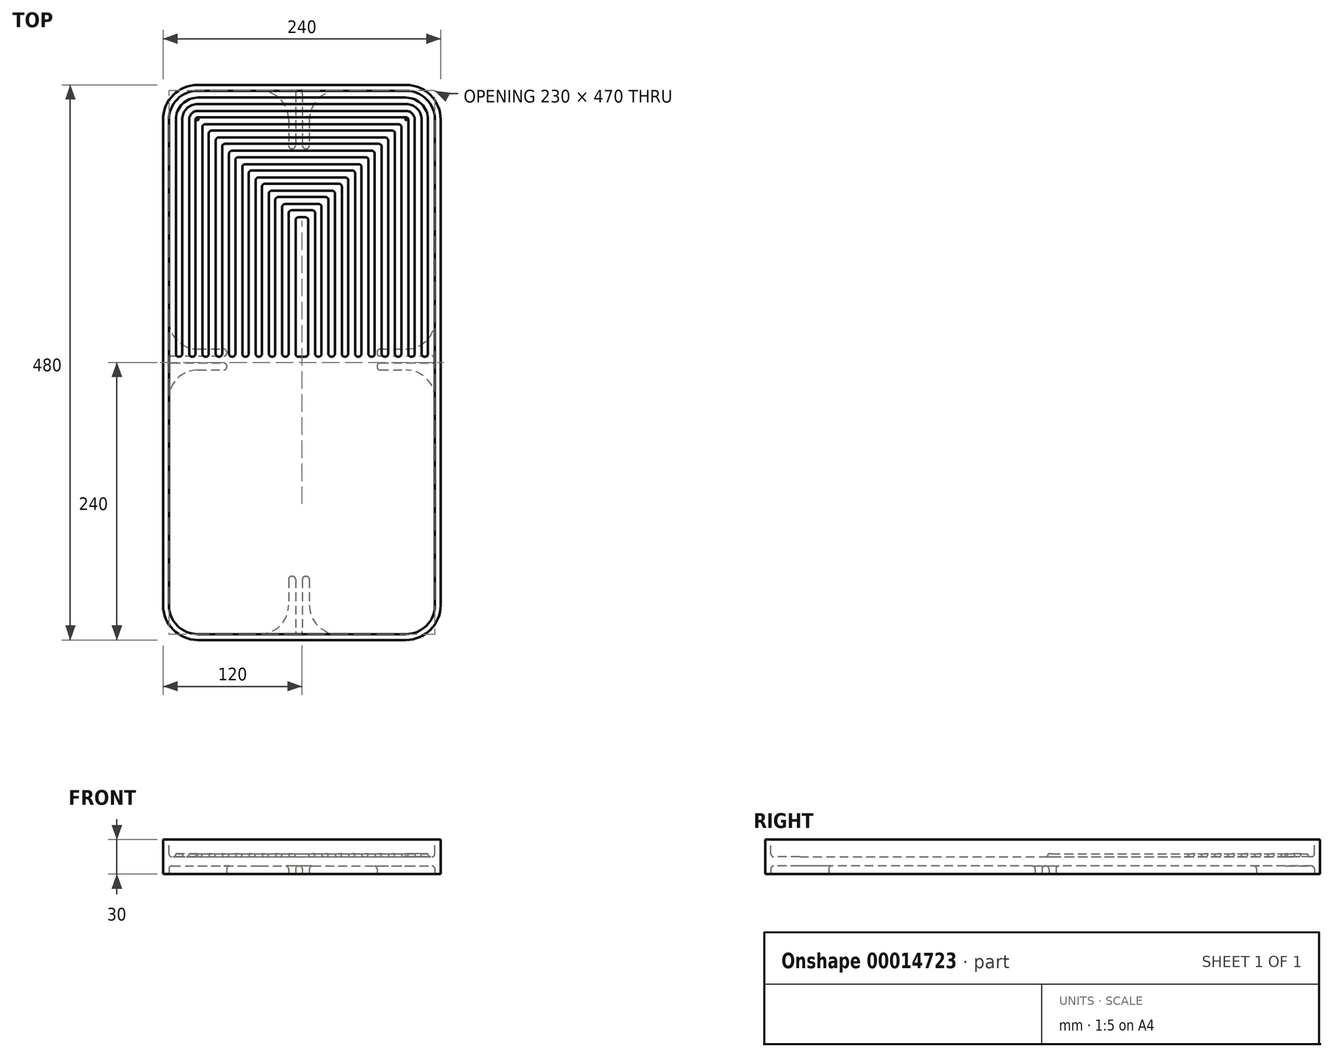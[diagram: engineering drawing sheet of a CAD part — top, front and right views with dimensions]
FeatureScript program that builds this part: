
annotation { "Feature Type Name" : "Feature", "Feature Type Description" : "" }
export const myFeature = defineFeature(function(context is Context, id is Id, definition is map)
    precondition{}
    {
        {
            var Q0;
            Q0=qCreatedBy(makeId("Top.planeOp"),FACE);
            var sketch = newSketch(context, id + "F0", { "sketchPlane" : qUnion([Q0])});
            skLineSegment(sketch, "E0.rect.bottom", {"start": v(-90, 240) * mm, "end": v(90, 240) * mm});
            skLineSegment(sketch, "E0.rect.top", {"start": v(-90, -240) * mm, "end": v(90, -240) * mm});
            skLineSegment(sketch, "E0.rect.left", {"start": v(-120, 210) * mm, "end": v(-120, -210) * mm});
            skLineSegment(sketch, "E0.rect.right", {"start": v(120, 210) * mm, "end": v(120, -210) * mm});
            skPoint(sketch, "E0.rect.middle", {"position": v(0, 0) * mm});
            skPoint(sketch, "E1.visualSharp", {"position": v(-120, 240) * mm});
            skArc(sketch, "E1.filletArc", {"start": v(-90, 240) * mm, "mid": v(-111.21, 231.21) * mm, "end": v(-120, 210) * mm});
            skPoint(sketch, "E2.visualSharp", {"position": v(120, 240) * mm});
            skArc(sketch, "E2.filletArc", {"start": v(120, 210) * mm, "mid": v(111.21, 231.21) * mm, "end": v(90, 240) * mm});
            skPoint(sketch, "E3.visualSharp", {"position": v(120, -240) * mm});
            skArc(sketch, "E3.filletArc", {"start": v(90, -240) * mm, "mid": v(111.21, -231.21) * mm, "end": v(120, -210) * mm});
            skPoint(sketch, "E4.visualSharp", {"position": v(-120, -240) * mm});
            skArc(sketch, "E4.filletArc", {"start": v(-120, -210) * mm, "mid": v(-111.21, -231.21) * mm, "end": v(-90, -240) * mm});
            skSolve(sketch);
        }
        {
            var Q0;
            Q0 = qSketchRegion(id + "F0", true);
            extrude(context, id + "F1", {"entities" : qUnion([Q0]), "depth" : 30 * mm});
        }
        {
            var Q0;
            Q0=makeQuery(id+"F1.opExtrude","CAP_FACE",FACE,{"disambiguationData":[OSD([sQuery(id+"F0.wireOp",EDGE,"E0.rect.bottom"),sQuery(id+"F0.wireOp",EDGE,"E0.rect.top"),sQuery(id+"F0.wireOp",EDGE,"E0.rect.left"),sQuery(id+"F0.wireOp",EDGE,"E0.rect.right"),sQuery(id+"F0.wireOp",EDGE,"E1.filletArc"),sQuery(id+"F0.wireOp",EDGE,"E2.filletArc"),sQuery(id+"F0.wireOp",EDGE,"E3.filletArc"),sQuery(id+"F0.wireOp",EDGE,"E4.filletArc")])],"isStart":true});
            var sketch = newSketch(context, id + "F2", { "sketchPlane" : qUnion([Q0])});
            skLineSegment(sketch, "E5.0", {"start": v(-90, -235) * mm, "end": v(-36.5, -235) * mm});
            skArc(sketch, "E5.1", {"start": v(115, -210) * mm, "mid": v(107.68, -227.68) * mm, "end": v(90, -235) * mm});
            skLineSegment(sketch, "E5.2", {"start": v(115, -210) * mm, "end": v(115, -36.5) * mm});
            skArc(sketch, "E5.3", {"start": v(90, 235) * mm, "mid": v(107.68, 227.68) * mm, "end": v(115, 210) * mm});
            skLineSegment(sketch, "E5.4", {"start": v(-90, 235) * mm, "end": v(-36.5, 235) * mm});
            skArc(sketch, "E5.5", {"start": v(-90, -235) * mm, "mid": v(-107.68, -227.68) * mm, "end": v(-115, -210) * mm});
            skArc(sketch, "E5.6", {"start": v(-115, 210) * mm, "mid": v(-107.68, 227.68) * mm, "end": v(-90, 235) * mm});
            skLineSegment(sketch, "E5.7", {"start": v(-115, -210) * mm, "end": v(-115, -36.5) * mm});
            skLineSegment(sketch, "E6", {"start": v(6.5, -210) * mm, "end": v(6.5, -187.5) * mm});
            skLineSegment(sketch, "E7.0", {"start": v(0.5, -232.5) * mm, "end": v(0.5, -187.5) * mm});
            skLineSegment(sketch, "E8.0", {"start": v(-5.5, -232.5) * mm, "end": v(-5.5, -187.5) * mm});
            skLineSegment(sketch, "E9.0", {"start": v(-11.5, -210) * mm, "end": v(-11.5, -187.5) * mm});
            skLineSegment(sketch, "E10.0", {"start": v(-9, -185) * mm, "end": v(-8, -185) * mm});
            skLineSegment(sketch, "E11.0", {"start": v(-9, 185) * mm, "end": v(-8, 185) * mm});
            skLineSegment(sketch, "E12.trimOffspring", {"start": v(-11.5, 187.5) * mm, "end": v(-11.5, 210) * mm});
            skLineSegment(sketch, "E13.trimOffspring", {"start": v(-5.5, 187.5) * mm, "end": v(-5.5, 232.5) * mm});
            skLineSegment(sketch, "E14.trimOffspring", {"start": v(0.5, 187.5) * mm, "end": v(0.5, 232.5) * mm});
            skLineSegment(sketch, "E15.trimOffspring", {"start": v(6.5, 187.5) * mm, "end": v(6.5, 210) * mm});
            skLineSegment(sketch, "E16.trimOffspring", {"start": v(3, 185) * mm, "end": v(4, 185) * mm});
            skLineSegment(sketch, "E17.trimOffspring", {"start": v(3, -185) * mm, "end": v(4, -185) * mm});
            skLineSegment(sketch, "E18.trimOffspring", {"start": v(-3, -235) * mm, "end": v(-2, -235) * mm});
            skLineSegment(sketch, "E19.trimOffspring", {"start": v(31.5, -235) * mm, "end": v(90, -235) * mm});
            skLineSegment(sketch, "E20.trimOffspring", {"start": v(-3, 235) * mm, "end": v(-2, 235) * mm});
            skLineSegment(sketch, "E21.trimOffspring", {"start": v(31.5, 235) * mm, "end": v(90, 235) * mm});
            skLineSegment(sketch, "E22", {"start": v(-90, -11.5) * mm, "end": v(-67.5, -11.5) * mm});
            skLineSegment(sketch, "E23.0", {"start": v(-112.5, -5.5) * mm, "end": v(-67.5, -5.5) * mm});
            skLineSegment(sketch, "E24.0", {"start": v(-112.5, 0.5) * mm, "end": v(-67.5, 0.5) * mm});
            skLineSegment(sketch, "E25.0", {"start": v(-90, 6.5) * mm, "end": v(-67.5, 6.5) * mm});
            skLineSegment(sketch, "E26.0", {"start": v(-65, -9) * mm, "end": v(-65, -8) * mm});
            skLineSegment(sketch, "E27.0", {"start": v(65, -9) * mm, "end": v(65, -8) * mm});
            skLineSegment(sketch, "E28.trimOffspring", {"start": v(67.5, 6.5) * mm, "end": v(90, 6.5) * mm});
            skLineSegment(sketch, "E29.trimOffspring", {"start": v(67.5, 0.5) * mm, "end": v(112.5, 0.5) * mm});
            skLineSegment(sketch, "E30.trimOffspring", {"start": v(67.5, -5.5) * mm, "end": v(112.5, -5.5) * mm});
            skLineSegment(sketch, "E31.trimOffspring", {"start": v(67.5, -11.5) * mm, "end": v(90, -11.5) * mm});
            skLineSegment(sketch, "E32.trimOffspring", {"start": v(65, 3) * mm, "end": v(65, 4) * mm});
            skLineSegment(sketch, "E33.trimOffspring", {"start": v(-65, 3) * mm, "end": v(-65, 4) * mm});
            skLineSegment(sketch, "E34.trimOffspring", {"start": v(-115, -3) * mm, "end": v(-115, -2) * mm});
            skLineSegment(sketch, "E35.trimOffspring", {"start": v(-115, 31.5) * mm, "end": v(-115, 210) * mm});
            skLineSegment(sketch, "E36.trimOffspring", {"start": v(115, -3) * mm, "end": v(115, -2) * mm});
            skLineSegment(sketch, "E37.trimOffspring", {"start": v(115, 31.5) * mm, "end": v(115, 210) * mm});
            skPoint(sketch, "E38.visualSharp", {"position": v(-11.5, -185) * mm});
            skArc(sketch, "E38.filletArc", {"start": v(-9, -185) * mm, "mid": v(-10.77, -185.73) * mm, "end": v(-11.5, -187.5) * mm});
            skPoint(sketch, "E39.visualSharp", {"position": v(-5.5, -185) * mm});
            skArc(sketch, "E39.filletArc", {"start": v(-5.5, -187.5) * mm, "mid": v(-6.23, -185.73) * mm, "end": v(-8, -185) * mm});
            skPoint(sketch, "E40.visualSharp", {"position": v(0.5, -185) * mm});
            skArc(sketch, "E40.filletArc", {"start": v(3, -185) * mm, "mid": v(1.23, -185.73) * mm, "end": v(0.5, -187.5) * mm});
            skPoint(sketch, "E41.visualSharp", {"position": v(6.5, -185) * mm});
            skArc(sketch, "E41.filletArc", {"start": v(6.5, -187.5) * mm, "mid": v(5.77, -185.73) * mm, "end": v(4, -185) * mm});
            skPoint(sketch, "E42.visualSharp", {"position": v(-5.5, -235) * mm});
            skArc(sketch, "E42.filletArc", {"start": v(-5.5, -232.5) * mm, "mid": v(-4.77, -234.27) * mm, "end": v(-3, -235) * mm});
            skPoint(sketch, "E43.visualSharp", {"position": v(0.5, -235) * mm});
            skArc(sketch, "E43.filletArc", {"start": v(-2, -235) * mm, "mid": v(-0.23, -234.27) * mm, "end": v(0.5, -232.5) * mm});
            skPoint(sketch, "E44.visualSharp", {"position": v(-5.5, 235) * mm});
            skArc(sketch, "E44.filletArc", {"start": v(-3, 235) * mm, "mid": v(-4.77, 234.27) * mm, "end": v(-5.5, 232.5) * mm});
            skPoint(sketch, "E45.visualSharp", {"position": v(0.5, 235) * mm});
            skArc(sketch, "E45.filletArc", {"start": v(0.5, 232.5) * mm, "mid": v(-0.23, 234.27) * mm, "end": v(-2, 235) * mm});
            skPoint(sketch, "E46.visualSharp", {"position": v(-11.5, 185) * mm});
            skArc(sketch, "E46.filletArc", {"start": v(-11.5, 187.5) * mm, "mid": v(-10.77, 185.73) * mm, "end": v(-9, 185) * mm});
            skPoint(sketch, "E47.visualSharp", {"position": v(-5.5, 185) * mm});
            skArc(sketch, "E47.filletArc", {"start": v(-8, 185) * mm, "mid": v(-6.23, 185.73) * mm, "end": v(-5.5, 187.5) * mm});
            skPoint(sketch, "E48.visualSharp", {"position": v(0.5, 185) * mm});
            skArc(sketch, "E48.filletArc", {"start": v(0.5, 187.5) * mm, "mid": v(1.23, 185.73) * mm, "end": v(3, 185) * mm});
            skPoint(sketch, "E49.visualSharp", {"position": v(6.5, 185) * mm});
            skArc(sketch, "E49.filletArc", {"start": v(4, 185) * mm, "mid": v(5.77, 185.73) * mm, "end": v(6.5, 187.5) * mm});
            skPoint(sketch, "E50.visualSharp", {"position": v(-65, 6.5) * mm});
            skArc(sketch, "E50.filletArc", {"start": v(-65, 4) * mm, "mid": v(-65.73, 5.77) * mm, "end": v(-67.5, 6.5) * mm});
            skPoint(sketch, "E51.visualSharp", {"position": v(-65, 0.5) * mm});
            skArc(sketch, "E51.filletArc", {"start": v(-67.5, 0.5) * mm, "mid": v(-65.73, 1.23) * mm, "end": v(-65, 3) * mm});
            skPoint(sketch, "E52.visualSharp", {"position": v(-115, 0.5) * mm});
            skArc(sketch, "E52.filletArc", {"start": v(-112.5, 0.5) * mm, "mid": v(-114.27, -0.23) * mm, "end": v(-115, -2) * mm});
            skPoint(sketch, "E53.visualSharp", {"position": v(-115, -5.5) * mm});
            skArc(sketch, "E53.filletArc", {"start": v(-115, -3) * mm, "mid": v(-114.27, -4.77) * mm, "end": v(-112.5, -5.5) * mm});
            skPoint(sketch, "E54.visualSharp", {"position": v(-65, -5.5) * mm});
            skArc(sketch, "E54.filletArc", {"start": v(-65, -8) * mm, "mid": v(-65.73, -6.23) * mm, "end": v(-67.5, -5.5) * mm});
            skPoint(sketch, "E55.visualSharp", {"position": v(-65, -11.5) * mm});
            skArc(sketch, "E55.filletArc", {"start": v(-67.5, -11.5) * mm, "mid": v(-65.73, -10.77) * mm, "end": v(-65, -9) * mm});
            skPoint(sketch, "E56.visualSharp", {"position": v(65, -11.5) * mm});
            skArc(sketch, "E56.filletArc", {"start": v(65, -9) * mm, "mid": v(65.73, -10.77) * mm, "end": v(67.5, -11.5) * mm});
            skPoint(sketch, "E57.visualSharp", {"position": v(65, -5.5) * mm});
            skArc(sketch, "E57.filletArc", {"start": v(67.5, -5.5) * mm, "mid": v(65.73, -6.23) * mm, "end": v(65, -8) * mm});
            skPoint(sketch, "E58.visualSharp", {"position": v(65, 0.5) * mm});
            skArc(sketch, "E58.filletArc", {"start": v(65, 3) * mm, "mid": v(65.73, 1.23) * mm, "end": v(67.5, 0.5) * mm});
            skPoint(sketch, "E59.visualSharp", {"position": v(65, 6.5) * mm});
            skArc(sketch, "E59.filletArc", {"start": v(67.5, 6.5) * mm, "mid": v(65.73, 5.77) * mm, "end": v(65, 4) * mm});
            skPoint(sketch, "E60.visualSharp", {"position": v(115, 0.5) * mm});
            skArc(sketch, "E60.filletArc", {"start": v(115, -2) * mm, "mid": v(114.27, -0.23) * mm, "end": v(112.5, 0.5) * mm});
            skPoint(sketch, "E61.visualSharp", {"position": v(115, -5.5) * mm});
            skArc(sketch, "E61.filletArc", {"start": v(112.5, -5.5) * mm, "mid": v(114.27, -4.77) * mm, "end": v(115, -3) * mm});
            skPoint(sketch, "E62.visualSharp", {"position": v(6.5, 235) * mm});
            skArc(sketch, "E62.filletArc", {"start": v(31.5, 235) * mm, "mid": v(13.82, 227.68) * mm, "end": v(6.5, 210) * mm});
            skPoint(sketch, "E63.visualSharp", {"position": v(-11.5, 235) * mm});
            skArc(sketch, "E63.filletArc", {"start": v(-11.5, 210) * mm, "mid": v(-18.82, 227.68) * mm, "end": v(-36.5, 235) * mm});
            skPoint(sketch, "E64.visualSharp", {"position": v(-115, 6.5) * mm});
            skArc(sketch, "E64.filletArc", {"start": v(-115, 31.5) * mm, "mid": v(-107.68, 13.82) * mm, "end": v(-90, 6.5) * mm});
            skPoint(sketch, "E65.visualSharp", {"position": v(-115, -11.5) * mm});
            skArc(sketch, "E65.filletArc", {"start": v(-90, -11.5) * mm, "mid": v(-107.68, -18.82) * mm, "end": v(-115, -36.5) * mm});
            skPoint(sketch, "E66.visualSharp", {"position": v(-11.5, -235) * mm});
            skArc(sketch, "E66.filletArc", {"start": v(-36.5, -235) * mm, "mid": v(-18.82, -227.68) * mm, "end": v(-11.5, -210) * mm});
            skPoint(sketch, "E67.visualSharp", {"position": v(6.5, -235) * mm});
            skArc(sketch, "E67.filletArc", {"start": v(6.5, -210) * mm, "mid": v(13.82, -227.68) * mm, "end": v(31.5, -235) * mm});
            skPoint(sketch, "E68.visualSharp", {"position": v(115, -11.5) * mm});
            skArc(sketch, "E68.filletArc", {"start": v(115, -36.5) * mm, "mid": v(107.68, -18.82) * mm, "end": v(90, -11.5) * mm});
            skPoint(sketch, "E69.visualSharp", {"position": v(115, 6.5) * mm});
            skArc(sketch, "E69.filletArc", {"start": v(90, 6.5) * mm, "mid": v(107.68, 13.82) * mm, "end": v(115, 31.5) * mm});
            skSolve(sketch);
        }
        {
            var Q0;
            Q0=makeQuery(id+"F2.imprint","IMPRINT",FACE,{"disambiguationData":[TD([[makeQuery(id+"F2.imprint","IMPRINT",EDGE,{"derivedFrom":sQuery(id+"F2.wireOp",EDGE,"E5.0")}),1.0]])]});
            extrude(context, id + "F3", {"entities" : qUnion([Q0]), "operationType" : NewBodyOperationType.REMOVE, "oppositeDirection" : true, "depth" : 7 * mm});
        }
        {
            var Q0;
            Q0=makeQuery(id+"F1.opExtrude","CAP_FACE",FACE,{"disambiguationData":[OSD([sQuery(id+"F0.wireOp",EDGE,"E0.rect.bottom"),sQuery(id+"F0.wireOp",EDGE,"E0.rect.top"),sQuery(id+"F0.wireOp",EDGE,"E0.rect.left"),sQuery(id+"F0.wireOp",EDGE,"E0.rect.right"),sQuery(id+"F0.wireOp",EDGE,"E1.filletArc"),sQuery(id+"F0.wireOp",EDGE,"E2.filletArc"),sQuery(id+"F0.wireOp",EDGE,"E3.filletArc"),sQuery(id+"F0.wireOp",EDGE,"E4.filletArc")])],"isStart":false});
            var sketch = newSketch(context, id + "F4", { "sketchPlane" : qUnion([Q0])});
            skLineSegment(sketch, "E70.rect.bottom", {"start": v(-90, -235) * mm, "end": v(90, -235) * mm});
            skLineSegment(sketch, "E70.rect.top", {"start": v(-90, 235) * mm, "end": v(90, 235) * mm});
            skLineSegment(sketch, "E70.rect.left", {"start": v(-115, -210) * mm, "end": v(-115, 210) * mm});
            skLineSegment(sketch, "E70.rect.right", {"start": v(115, -210) * mm, "end": v(115, 210) * mm});
            skPoint(sketch, "E70.rect.middle", {"position": v(0, 0) * mm});
            skPoint(sketch, "E71.visualSharp", {"position": v(-115, -235) * mm});
            skArc(sketch, "E71.filletArc", {"start": v(-115, -210) * mm, "mid": v(-107.68, -227.68) * mm, "end": v(-90, -235) * mm});
            skPoint(sketch, "E72.visualSharp", {"position": v(-115, 235) * mm});
            skArc(sketch, "E72.filletArc", {"start": v(-90, 235) * mm, "mid": v(-107.68, 227.68) * mm, "end": v(-115, 210) * mm});
            skPoint(sketch, "E73.visualSharp", {"position": v(115, 235) * mm});
            skArc(sketch, "E73.filletArc", {"start": v(115, 210) * mm, "mid": v(107.68, 227.68) * mm, "end": v(90, 235) * mm});
            skPoint(sketch, "E74.visualSharp", {"position": v(115, -235) * mm});
            skArc(sketch, "E74.filletArc", {"start": v(90, -235) * mm, "mid": v(107.68, -227.68) * mm, "end": v(115, -210) * mm});
            skSolve(sketch);
        }
        {
            var Q0;
            Q0 = qSketchRegion(id + "F4", true);
            extrude(context, id + "F5", {"entities" : qUnion([Q0]), "operationType" : NewBodyOperationType.REMOVE, "oppositeDirection" : true, "depth" : 12.5 * mm});
        }
        {
            var Q0;
            Q0=makeQuery(id+"F5.boolean.opBoolean","COPY",FACE,{"derivedFrom":makeQuery(id+"F5.opExtrude","CAP_FACE",FACE,{"disambiguationData":[OSD([sQuery(id+"F4.wireOp",EDGE,"E70.rect.bottom"),sQuery(id+"F4.wireOp",EDGE,"E70.rect.top"),sQuery(id+"F4.wireOp",EDGE,"E70.rect.left"),sQuery(id+"F4.wireOp",EDGE,"E70.rect.right"),sQuery(id+"F4.wireOp",EDGE,"E71.filletArc"),sQuery(id+"F4.wireOp",EDGE,"E72.filletArc"),sQuery(id+"F4.wireOp",EDGE,"E73.filletArc"),sQuery(id+"F4.wireOp",EDGE,"E74.filletArc")])],"isStart":false})});
            var sketch = newSketch(context, id + "F6", { "sketchPlane" : qUnion([Q0])});
            skArc(sketch, "E75.0", {"start": v(-115, -210) * mm, "mid": v(-107.68, -227.68) * mm, "end": v(-90, -235) * mm});
            skLineSegment(sketch, "E75.1", {"start": v(-115, -210) * mm, "end": v(-115, 5) * mm});
            skArc(sketch, "E75.2", {"start": v(-90, 235) * mm, "mid": v(-107.68, 227.68) * mm, "end": v(-115, 210) * mm});
            skLineSegment(sketch, "E75.3", {"start": v(-90, 235) * mm, "end": v(90, 235) * mm});
            skArc(sketch, "E75.4", {"start": v(115, 210) * mm, "mid": v(107.68, 227.68) * mm, "end": v(90, 235) * mm});
            skLineSegment(sketch, "E75.5", {"start": v(115, -210) * mm, "end": v(115, 5) * mm});
            skArc(sketch, "E75.6", {"start": v(90, -235) * mm, "mid": v(107.68, -227.68) * mm, "end": v(115, -210) * mm});
            skLineSegment(sketch, "E75.7", {"start": v(-90, -235) * mm, "end": v(90, -235) * mm});
            skLineSegment(sketch, "E76.0", {"start": v(-106.5, 5) * mm, "end": v(-106, 5) * mm});
            skLineSegment(sketch, "E77", {"start": v(-115, 5) * mm, "end": v(-115, 210) * mm});
            skLineSegment(sketch, "E78", {"start": v(115, 5) * mm, "end": v(115, 210) * mm});
            skLineSegment(sketch, "E79.0", {"start": v(109, 7.5) * mm, "end": v(109, 210) * mm});
            skArc(sketch, "E79.1", {"start": v(109, 210) * mm, "mid": v(103.44, 223.44) * mm, "end": v(90, 229) * mm});
            skLineSegment(sketch, "E79.2", {"start": v(-90, 229) * mm, "end": v(90, 229) * mm});
            skArc(sketch, "E79.3", {"start": v(-90, 229) * mm, "mid": v(-103.44, 223.44) * mm, "end": v(-109, 210) * mm});
            skLineSegment(sketch, "E79.4", {"start": v(-109, 7.5) * mm, "end": v(-109, 210) * mm});
            skLineSegment(sketch, "E80.0", {"start": v(103.5, 7.5) * mm, "end": v(103.5, 210) * mm});
            skArc(sketch, "E80.1", {"start": v(103.5, 210) * mm, "mid": v(99.55, 219.55) * mm, "end": v(90, 223.5) * mm});
            skLineSegment(sketch, "E80.2", {"start": v(-90, 223.5) * mm, "end": v(90, 223.5) * mm});
            skArc(sketch, "E80.3", {"start": v(-90, 223.5) * mm, "mid": v(-99.55, 219.55) * mm, "end": v(-103.5, 210) * mm});
            skLineSegment(sketch, "E80.4", {"start": v(-103.5, 7.5) * mm, "end": v(-103.5, 210) * mm});
            skLineSegment(sketch, "E81.0", {"start": v(97.5, 7.5) * mm, "end": v(97.5, 210) * mm});
            skArc(sketch, "E81.1", {"start": v(97.5, 210) * mm, "mid": v(95.3, 215.3) * mm, "end": v(90, 217.5) * mm});
            skLineSegment(sketch, "E81.2", {"start": v(-90, 217.5) * mm, "end": v(90, 217.5) * mm});
            skArc(sketch, "E81.3", {"start": v(-90, 217.5) * mm, "mid": v(-95.3, 215.3) * mm, "end": v(-97.5, 210) * mm});
            skLineSegment(sketch, "E81.4", {"start": v(-97.5, 7.5) * mm, "end": v(-97.5, 210) * mm});
            skLineSegment(sketch, "E82.0", {"start": v(92, 7.5) * mm, "end": v(92, 210) * mm});
            skArc(sketch, "E82.1", {"start": v(92, 210) * mm, "mid": v(91.41, 211.41) * mm, "end": v(90, 212) * mm});
            skLineSegment(sketch, "E82.2", {"start": v(-90, 212) * mm, "end": v(90, 212) * mm});
            skArc(sketch, "E82.3", {"start": v(-90, 212) * mm, "mid": v(-91.41, 211.41) * mm, "end": v(-92, 210) * mm});
            skLineSegment(sketch, "E82.4", {"start": v(-92, 7.5) * mm, "end": v(-92, 210) * mm});
            skLineSegment(sketch, "E83.0", {"start": v(86, 7.5) * mm, "end": v(86, 203.5) * mm});
            skLineSegment(sketch, "E83.1", {"start": v(-83.5, 206) * mm, "end": v(83.5, 206) * mm});
            skLineSegment(sketch, "E83.2", {"start": v(-86, 7.5) * mm, "end": v(-86, 203.5) * mm});
            skLineSegment(sketch, "E84.0", {"start": v(80.5, 7.5) * mm, "end": v(80.5, 198) * mm});
            skLineSegment(sketch, "E84.1", {"start": v(-78, 200.5) * mm, "end": v(78, 200.5) * mm});
            skLineSegment(sketch, "E84.2", {"start": v(-80.5, 7.5) * mm, "end": v(-80.5, 198) * mm});
            skLineSegment(sketch, "E85.0", {"start": v(74.5, 7.5) * mm, "end": v(74.5, 192) * mm});
            skLineSegment(sketch, "E85.1", {"start": v(-72, 194.5) * mm, "end": v(72, 194.5) * mm});
            skLineSegment(sketch, "E85.2", {"start": v(-74.5, 7.5) * mm, "end": v(-74.5, 192) * mm});
            skLineSegment(sketch, "E86.0", {"start": v(69, 7.5) * mm, "end": v(69, 186.5) * mm});
            skLineSegment(sketch, "E86.1", {"start": v(-66.5, 189) * mm, "end": v(66.5, 189) * mm});
            skLineSegment(sketch, "E86.2", {"start": v(-69, 7.5) * mm, "end": v(-69, 186.5) * mm});
            skLineSegment(sketch, "E87.0", {"start": v(63, 7.5) * mm, "end": v(63, 180.5) * mm});
            skLineSegment(sketch, "E87.1", {"start": v(-60.5, 183) * mm, "end": v(60.5, 183) * mm});
            skLineSegment(sketch, "E87.2", {"start": v(-63, 7.5) * mm, "end": v(-63, 180.5) * mm});
            skLineSegment(sketch, "E88.0", {"start": v(57.5, 7.5) * mm, "end": v(57.5, 175) * mm});
            skLineSegment(sketch, "E88.1", {"start": v(-55, 177.5) * mm, "end": v(55, 177.5) * mm});
            skLineSegment(sketch, "E88.2", {"start": v(-57.5, 7.5) * mm, "end": v(-57.5, 175) * mm});
            skLineSegment(sketch, "E89.0", {"start": v(51.5, 7.5) * mm, "end": v(51.5, 169) * mm});
            skLineSegment(sketch, "E89.1", {"start": v(-49, 171.5) * mm, "end": v(49, 171.5) * mm});
            skLineSegment(sketch, "E89.2", {"start": v(-51.5, 7.5) * mm, "end": v(-51.5, 169) * mm});
            skLineSegment(sketch, "E90.0", {"start": v(46, 7.5) * mm, "end": v(46, 163.5) * mm});
            skLineSegment(sketch, "E90.1", {"start": v(-43.5, 166) * mm, "end": v(43.5, 166) * mm});
            skLineSegment(sketch, "E90.2", {"start": v(-46, 7.5) * mm, "end": v(-46, 163.5) * mm});
            skLineSegment(sketch, "E91.0", {"start": v(40, 7.5) * mm, "end": v(40, 157.5) * mm});
            skLineSegment(sketch, "E91.1", {"start": v(-37.5, 160) * mm, "end": v(37.5, 160) * mm});
            skLineSegment(sketch, "E91.2", {"start": v(-40, 7.5) * mm, "end": v(-40, 157.5) * mm});
            skLineSegment(sketch, "E92.0", {"start": v(34.5, 7.5) * mm, "end": v(34.5, 152) * mm});
            skLineSegment(sketch, "E92.1", {"start": v(-32, 154.5) * mm, "end": v(32, 154.5) * mm});
            skLineSegment(sketch, "E92.2", {"start": v(-34.5, 7.5) * mm, "end": v(-34.5, 152) * mm});
            skLineSegment(sketch, "E93.0", {"start": v(28.5, 7.5) * mm, "end": v(28.5, 146) * mm});
            skLineSegment(sketch, "E93.1", {"start": v(-26, 148.5) * mm, "end": v(26, 148.5) * mm});
            skLineSegment(sketch, "E93.2", {"start": v(-28.5, 7.5) * mm, "end": v(-28.5, 146) * mm});
            skLineSegment(sketch, "E94.0", {"start": v(23, 7.5) * mm, "end": v(23, 140.5) * mm});
            skLineSegment(sketch, "E94.1", {"start": v(-20.5, 143) * mm, "end": v(20.5, 143) * mm});
            skLineSegment(sketch, "E94.2", {"start": v(-23, 7.5) * mm, "end": v(-23, 140.5) * mm});
            skLineSegment(sketch, "E95.0", {"start": v(17, 7.5) * mm, "end": v(17, 134.5) * mm});
            skLineSegment(sketch, "E95.1", {"start": v(-14.5, 137) * mm, "end": v(14.5, 137) * mm});
            skLineSegment(sketch, "E95.2", {"start": v(-17, 7.5) * mm, "end": v(-17, 134.5) * mm});
            skLineSegment(sketch, "E96.0", {"start": v(11.5, 7.5) * mm, "end": v(11.5, 129) * mm});
            skLineSegment(sketch, "E96.1", {"start": v(-9, 131.5) * mm, "end": v(9, 131.5) * mm});
            skLineSegment(sketch, "E96.2", {"start": v(-11.5, 7.5) * mm, "end": v(-11.5, 129) * mm});
            skPoint(sketch, "E97.orphan", {"position": v(-115, 5) * mm});
            skLineSegment(sketch, "E98.trimOffspring", {"start": v(-95, 5) * mm, "end": v(-94.5, 5) * mm});
            skLineSegment(sketch, "E99.trimOffspring", {"start": v(-83.5, 5) * mm, "end": v(-83, 5) * mm});
            skLineSegment(sketch, "E100.trimOffspring", {"start": v(-72, 5) * mm, "end": v(-71.5, 5) * mm});
            skLineSegment(sketch, "E101.trimOffspring", {"start": v(-60.5, 5) * mm, "end": v(-60, 5) * mm});
            skLineSegment(sketch, "E102.trimOffspring", {"start": v(-49, 5) * mm, "end": v(-48.5, 5) * mm});
            skLineSegment(sketch, "E103.trimOffspring", {"start": v(-37.5, 5) * mm, "end": v(-37, 5) * mm});
            skLineSegment(sketch, "E104.trimOffspring", {"start": v(-26, 5) * mm, "end": v(-25.5, 5) * mm});
            skLineSegment(sketch, "E105.trimOffspring", {"start": v(-14.5, 5) * mm, "end": v(-14, 5) * mm});
            skLineSegment(sketch, "E106.trimOffspring", {"start": v(106, 5) * mm, "end": v(106.5, 5) * mm});
            skLineSegment(sketch, "E107.trimOffspring", {"start": v(94.5, 5) * mm, "end": v(95, 5) * mm});
            skLineSegment(sketch, "E108.trimOffspring", {"start": v(83, 5) * mm, "end": v(83.5, 5) * mm});
            skLineSegment(sketch, "E109.trimOffspring", {"start": v(71.5, 5) * mm, "end": v(72, 5) * mm});
            skLineSegment(sketch, "E110.trimOffspring", {"start": v(60, 5) * mm, "end": v(60.5, 5) * mm});
            skLineSegment(sketch, "E111.trimOffspring", {"start": v(48.5, 5) * mm, "end": v(49, 5) * mm});
            skLineSegment(sketch, "E112.trimOffspring", {"start": v(37, 5) * mm, "end": v(37.5, 5) * mm});
            skLineSegment(sketch, "E113.trimOffspring", {"start": v(25.5, 5) * mm, "end": v(26, 5) * mm});
            skLineSegment(sketch, "E114.0", {"start": v(5.5, 7.5) * mm, "end": v(5.5, 123) * mm});
            skLineSegment(sketch, "E114.1", {"start": v(-3, 125.5) * mm, "end": v(3, 125.5) * mm});
            skLineSegment(sketch, "E114.2", {"start": v(-5.5, 7.5) * mm, "end": v(-5.5, 123) * mm});
            skLineSegment(sketch, "E115.trimOffspring", {"start": v(14, 5) * mm, "end": v(14.5, 5) * mm});
            skLineSegment(sketch, "E116.trimOffspring", {"start": v(-3, 5) * mm, "end": v(3, 5) * mm});
            skPoint(sketch, "E117.visualSharp", {"position": v(-5.5, 5) * mm});
            skArc(sketch, "E117.filletArc", {"start": v(-5.5, 7.5) * mm, "mid": v(-4.77, 5.73) * mm, "end": v(-3, 5) * mm});
            skPoint(sketch, "E118.visualSharp", {"position": v(5.5, 5) * mm});
            skArc(sketch, "E118.filletArc", {"start": v(3, 5) * mm, "mid": v(4.77, 5.73) * mm, "end": v(5.5, 7.5) * mm});
            skPoint(sketch, "E119.visualSharp", {"position": v(-11.5, 5) * mm});
            skArc(sketch, "E119.filletArc", {"start": v(-14, 5) * mm, "mid": v(-12.23, 5.73) * mm, "end": v(-11.5, 7.5) * mm});
            skPoint(sketch, "E120.visualSharp", {"position": v(-17, 5) * mm});
            skArc(sketch, "E120.filletArc", {"start": v(-17, 7.5) * mm, "mid": v(-16.27, 5.73) * mm, "end": v(-14.5, 5) * mm});
            skPoint(sketch, "E121.visualSharp", {"position": v(-23, 5) * mm});
            skArc(sketch, "E121.filletArc", {"start": v(-25.5, 5) * mm, "mid": v(-23.73, 5.73) * mm, "end": v(-23, 7.5) * mm});
            skPoint(sketch, "E122.visualSharp", {"position": v(-28.5, 5) * mm});
            skArc(sketch, "E122.filletArc", {"start": v(-28.5, 7.5) * mm, "mid": v(-27.77, 5.73) * mm, "end": v(-26, 5) * mm});
            skPoint(sketch, "E123.visualSharp", {"position": v(-34.5, 5) * mm});
            skArc(sketch, "E123.filletArc", {"start": v(-37, 5) * mm, "mid": v(-35.23, 5.73) * mm, "end": v(-34.5, 7.5) * mm});
            skPoint(sketch, "E124.visualSharp", {"position": v(-40, 5) * mm});
            skArc(sketch, "E124.filletArc", {"start": v(-40, 7.5) * mm, "mid": v(-39.27, 5.73) * mm, "end": v(-37.5, 5) * mm});
            skPoint(sketch, "E125.visualSharp", {"position": v(-46, 5) * mm});
            skArc(sketch, "E125.filletArc", {"start": v(-48.5, 5) * mm, "mid": v(-46.73, 5.73) * mm, "end": v(-46, 7.5) * mm});
            skPoint(sketch, "E126.visualSharp", {"position": v(-51.5, 5) * mm});
            skArc(sketch, "E126.filletArc", {"start": v(-51.5, 7.5) * mm, "mid": v(-50.77, 5.73) * mm, "end": v(-49, 5) * mm});
            skPoint(sketch, "E127.visualSharp", {"position": v(-57.5, 5) * mm});
            skArc(sketch, "E127.filletArc", {"start": v(-60, 5) * mm, "mid": v(-58.23, 5.73) * mm, "end": v(-57.5, 7.5) * mm});
            skPoint(sketch, "E128.visualSharp", {"position": v(-63, 5) * mm});
            skArc(sketch, "E128.filletArc", {"start": v(-63, 7.5) * mm, "mid": v(-62.27, 5.73) * mm, "end": v(-60.5, 5) * mm});
            skPoint(sketch, "E129.visualSharp", {"position": v(-69, 5) * mm});
            skArc(sketch, "E129.filletArc", {"start": v(-71.5, 5) * mm, "mid": v(-69.73, 5.73) * mm, "end": v(-69, 7.5) * mm});
            skPoint(sketch, "E130.visualSharp", {"position": v(-74.5, 5) * mm});
            skArc(sketch, "E130.filletArc", {"start": v(-74.5, 7.5) * mm, "mid": v(-73.77, 5.73) * mm, "end": v(-72, 5) * mm});
            skPoint(sketch, "E131.visualSharp", {"position": v(-80.5, 5) * mm});
            skArc(sketch, "E131.filletArc", {"start": v(-83, 5) * mm, "mid": v(-81.23, 5.73) * mm, "end": v(-80.5, 7.5) * mm});
            skPoint(sketch, "E132.visualSharp", {"position": v(-86, 5) * mm});
            skArc(sketch, "E132.filletArc", {"start": v(-86, 7.5) * mm, "mid": v(-85.27, 5.73) * mm, "end": v(-83.5, 5) * mm});
            skPoint(sketch, "E133.visualSharp", {"position": v(-92, 5) * mm});
            skArc(sketch, "E133.filletArc", {"start": v(-94.5, 5) * mm, "mid": v(-92.73, 5.73) * mm, "end": v(-92, 7.5) * mm});
            skPoint(sketch, "E134.visualSharp", {"position": v(-97.5, 5) * mm});
            skArc(sketch, "E134.filletArc", {"start": v(-97.5, 7.5) * mm, "mid": v(-96.77, 5.73) * mm, "end": v(-95, 5) * mm});
            skPoint(sketch, "E135.visualSharp", {"position": v(-103.5, 5) * mm});
            skArc(sketch, "E135.filletArc", {"start": v(-106, 5) * mm, "mid": v(-104.23, 5.73) * mm, "end": v(-103.5, 7.5) * mm});
            skPoint(sketch, "E136.visualSharp", {"position": v(-109, 5) * mm});
            skArc(sketch, "E136.filletArc", {"start": v(-109, 7.5) * mm, "mid": v(-108.27, 5.73) * mm, "end": v(-106.5, 5) * mm});
            skPoint(sketch, "E137.visualSharp", {"position": v(-86, 206) * mm});
            skArc(sketch, "E137.filletArc", {"start": v(-83.5, 206) * mm, "mid": v(-85.27, 205.27) * mm, "end": v(-86, 203.5) * mm});
            skPoint(sketch, "E138.visualSharp", {"position": v(-80.5, 200.5) * mm});
            skArc(sketch, "E138.filletArc", {"start": v(-78, 200.5) * mm, "mid": v(-79.77, 199.77) * mm, "end": v(-80.5, 198) * mm});
            skPoint(sketch, "E139.visualSharp", {"position": v(-74.5, 194.5) * mm});
            skArc(sketch, "E139.filletArc", {"start": v(-72, 194.5) * mm, "mid": v(-73.77, 193.77) * mm, "end": v(-74.5, 192) * mm});
            skPoint(sketch, "E140.visualSharp", {"position": v(-69, 189) * mm});
            skArc(sketch, "E140.filletArc", {"start": v(-66.5, 189) * mm, "mid": v(-68.27, 188.27) * mm, "end": v(-69, 186.5) * mm});
            skPoint(sketch, "E141.visualSharp", {"position": v(-63, 183) * mm});
            skArc(sketch, "E141.filletArc", {"start": v(-60.5, 183) * mm, "mid": v(-62.27, 182.27) * mm, "end": v(-63, 180.5) * mm});
            skPoint(sketch, "E142.visualSharp", {"position": v(-57.5, 177.5) * mm});
            skArc(sketch, "E142.filletArc", {"start": v(-55, 177.5) * mm, "mid": v(-56.77, 176.77) * mm, "end": v(-57.5, 175) * mm});
            skPoint(sketch, "E143.visualSharp", {"position": v(-51.5, 171.5) * mm});
            skArc(sketch, "E143.filletArc", {"start": v(-49, 171.5) * mm, "mid": v(-50.77, 170.77) * mm, "end": v(-51.5, 169) * mm});
            skPoint(sketch, "E144.visualSharp", {"position": v(-46, 166) * mm});
            skArc(sketch, "E144.filletArc", {"start": v(-43.5, 166) * mm, "mid": v(-45.27, 165.27) * mm, "end": v(-46, 163.5) * mm});
            skPoint(sketch, "E145.visualSharp", {"position": v(-40, 160) * mm});
            skArc(sketch, "E145.filletArc", {"start": v(-37.5, 160) * mm, "mid": v(-39.27, 159.27) * mm, "end": v(-40, 157.5) * mm});
            skPoint(sketch, "E146.visualSharp", {"position": v(-34.5, 154.5) * mm});
            skArc(sketch, "E146.filletArc", {"start": v(-32, 154.5) * mm, "mid": v(-33.77, 153.77) * mm, "end": v(-34.5, 152) * mm});
            skPoint(sketch, "E147.visualSharp", {"position": v(-28.5, 148.5) * mm});
            skArc(sketch, "E147.filletArc", {"start": v(-26, 148.5) * mm, "mid": v(-27.77, 147.77) * mm, "end": v(-28.5, 146) * mm});
            skPoint(sketch, "E148.visualSharp", {"position": v(-23, 143) * mm});
            skArc(sketch, "E148.filletArc", {"start": v(-20.5, 143) * mm, "mid": v(-22.27, 142.27) * mm, "end": v(-23, 140.5) * mm});
            skPoint(sketch, "E149.visualSharp", {"position": v(-17, 137) * mm});
            skArc(sketch, "E149.filletArc", {"start": v(-14.5, 137) * mm, "mid": v(-16.27, 136.27) * mm, "end": v(-17, 134.5) * mm});
            skPoint(sketch, "E150.visualSharp", {"position": v(-11.5, 131.5) * mm});
            skArc(sketch, "E150.filletArc", {"start": v(-9, 131.5) * mm, "mid": v(-10.77, 130.77) * mm, "end": v(-11.5, 129) * mm});
            skPoint(sketch, "E151.visualSharp", {"position": v(-5.5, 125.5) * mm});
            skArc(sketch, "E151.filletArc", {"start": v(-3, 125.5) * mm, "mid": v(-4.77, 124.77) * mm, "end": v(-5.5, 123) * mm});
            skPoint(sketch, "E152.visualSharp", {"position": v(5.5, 125.5) * mm});
            skArc(sketch, "E152.filletArc", {"start": v(5.5, 123) * mm, "mid": v(4.77, 124.77) * mm, "end": v(3, 125.5) * mm});
            skPoint(sketch, "E153.visualSharp", {"position": v(11.5, 131.5) * mm});
            skArc(sketch, "E153.filletArc", {"start": v(11.5, 129) * mm, "mid": v(10.77, 130.77) * mm, "end": v(9, 131.5) * mm});
            skPoint(sketch, "E154.visualSharp", {"position": v(17, 137) * mm});
            skArc(sketch, "E154.filletArc", {"start": v(17, 134.5) * mm, "mid": v(16.27, 136.27) * mm, "end": v(14.5, 137) * mm});
            skPoint(sketch, "E155.visualSharp", {"position": v(23, 143) * mm});
            skArc(sketch, "E155.filletArc", {"start": v(23, 140.5) * mm, "mid": v(22.27, 142.27) * mm, "end": v(20.5, 143) * mm});
            skPoint(sketch, "E156.visualSharp", {"position": v(28.5, 148.5) * mm});
            skArc(sketch, "E156.filletArc", {"start": v(28.5, 146) * mm, "mid": v(27.77, 147.77) * mm, "end": v(26, 148.5) * mm});
            skPoint(sketch, "E157.visualSharp", {"position": v(34.5, 154.5) * mm});
            skArc(sketch, "E157.filletArc", {"start": v(34.5, 152) * mm, "mid": v(33.77, 153.77) * mm, "end": v(32, 154.5) * mm});
            skPoint(sketch, "E158.visualSharp", {"position": v(40, 160) * mm});
            skArc(sketch, "E158.filletArc", {"start": v(40, 157.5) * mm, "mid": v(39.27, 159.27) * mm, "end": v(37.5, 160) * mm});
            skPoint(sketch, "E159.visualSharp", {"position": v(46, 166) * mm});
            skArc(sketch, "E159.filletArc", {"start": v(46, 163.5) * mm, "mid": v(45.27, 165.27) * mm, "end": v(43.5, 166) * mm});
            skPoint(sketch, "E160.visualSharp", {"position": v(51.5, 171.5) * mm});
            skArc(sketch, "E160.filletArc", {"start": v(51.5, 169) * mm, "mid": v(50.77, 170.77) * mm, "end": v(49, 171.5) * mm});
            skPoint(sketch, "E161.visualSharp", {"position": v(57.5, 177.5) * mm});
            skArc(sketch, "E161.filletArc", {"start": v(57.5, 175) * mm, "mid": v(56.77, 176.77) * mm, "end": v(55, 177.5) * mm});
            skPoint(sketch, "E162.visualSharp", {"position": v(63, 183) * mm});
            skArc(sketch, "E162.filletArc", {"start": v(63, 180.5) * mm, "mid": v(62.27, 182.27) * mm, "end": v(60.5, 183) * mm});
            skPoint(sketch, "E163.visualSharp", {"position": v(69, 189) * mm});
            skArc(sketch, "E163.filletArc", {"start": v(69, 186.5) * mm, "mid": v(68.27, 188.27) * mm, "end": v(66.5, 189) * mm});
            skPoint(sketch, "E164.visualSharp", {"position": v(74.5, 194.5) * mm});
            skArc(sketch, "E164.filletArc", {"start": v(74.5, 192) * mm, "mid": v(73.77, 193.77) * mm, "end": v(72, 194.5) * mm});
            skPoint(sketch, "E165.visualSharp", {"position": v(80.5, 200.5) * mm});
            skArc(sketch, "E165.filletArc", {"start": v(80.5, 198) * mm, "mid": v(79.77, 199.77) * mm, "end": v(78, 200.5) * mm});
            skPoint(sketch, "E166.visualSharp", {"position": v(86, 206) * mm});
            skArc(sketch, "E166.filletArc", {"start": v(86, 203.5) * mm, "mid": v(85.27, 205.27) * mm, "end": v(83.5, 206) * mm});
            skPoint(sketch, "E167.visualSharp", {"position": v(109, 5) * mm});
            skArc(sketch, "E167.filletArc", {"start": v(106.5, 5) * mm, "mid": v(108.27, 5.73) * mm, "end": v(109, 7.5) * mm});
            skPoint(sketch, "E168.visualSharp", {"position": v(103.5, 5) * mm});
            skArc(sketch, "E168.filletArc", {"start": v(103.5, 7.5) * mm, "mid": v(104.23, 5.73) * mm, "end": v(106, 5) * mm});
            skPoint(sketch, "E169.visualSharp", {"position": v(97.5, 5) * mm});
            skArc(sketch, "E169.filletArc", {"start": v(95, 5) * mm, "mid": v(96.77, 5.73) * mm, "end": v(97.5, 7.5) * mm});
            skPoint(sketch, "E170.visualSharp", {"position": v(92, 5) * mm});
            skArc(sketch, "E170.filletArc", {"start": v(92, 7.5) * mm, "mid": v(92.73, 5.73) * mm, "end": v(94.5, 5) * mm});
            skPoint(sketch, "E171.visualSharp", {"position": v(86, 5) * mm});
            skArc(sketch, "E171.filletArc", {"start": v(83.5, 5) * mm, "mid": v(85.27, 5.73) * mm, "end": v(86, 7.5) * mm});
            skPoint(sketch, "E172.visualSharp", {"position": v(80.5, 5) * mm});
            skArc(sketch, "E172.filletArc", {"start": v(80.5, 7.5) * mm, "mid": v(81.23, 5.73) * mm, "end": v(83, 5) * mm});
            skPoint(sketch, "E173.visualSharp", {"position": v(74.5, 5) * mm});
            skArc(sketch, "E173.filletArc", {"start": v(72, 5) * mm, "mid": v(73.77, 5.73) * mm, "end": v(74.5, 7.5) * mm});
            skPoint(sketch, "E174.visualSharp", {"position": v(69, 5) * mm});
            skArc(sketch, "E174.filletArc", {"start": v(69, 7.5) * mm, "mid": v(69.73, 5.73) * mm, "end": v(71.5, 5) * mm});
            skPoint(sketch, "E175.visualSharp", {"position": v(63, 5) * mm});
            skArc(sketch, "E175.filletArc", {"start": v(60.5, 5) * mm, "mid": v(62.27, 5.73) * mm, "end": v(63, 7.5) * mm});
            skPoint(sketch, "E176.visualSharp", {"position": v(57.5, 5) * mm});
            skArc(sketch, "E176.filletArc", {"start": v(57.5, 7.5) * mm, "mid": v(58.23, 5.73) * mm, "end": v(60, 5) * mm});
            skPoint(sketch, "E177.visualSharp", {"position": v(51.5, 5) * mm});
            skArc(sketch, "E177.filletArc", {"start": v(49, 5) * mm, "mid": v(50.77, 5.73) * mm, "end": v(51.5, 7.5) * mm});
            skPoint(sketch, "E178.visualSharp", {"position": v(46, 5) * mm});
            skArc(sketch, "E178.filletArc", {"start": v(46, 7.5) * mm, "mid": v(46.73, 5.73) * mm, "end": v(48.5, 5) * mm});
            skPoint(sketch, "E179.visualSharp", {"position": v(40, 5) * mm});
            skArc(sketch, "E179.filletArc", {"start": v(37.5, 5) * mm, "mid": v(39.27, 5.73) * mm, "end": v(40, 7.5) * mm});
            skPoint(sketch, "E180.visualSharp", {"position": v(34.5, 5) * mm});
            skArc(sketch, "E180.filletArc", {"start": v(34.5, 7.5) * mm, "mid": v(35.23, 5.73) * mm, "end": v(37, 5) * mm});
            skPoint(sketch, "E181.visualSharp", {"position": v(28.5, 5) * mm});
            skArc(sketch, "E181.filletArc", {"start": v(26, 5) * mm, "mid": v(27.77, 5.73) * mm, "end": v(28.5, 7.5) * mm});
            skPoint(sketch, "E182.visualSharp", {"position": v(23, 5) * mm});
            skArc(sketch, "E182.filletArc", {"start": v(23, 7.5) * mm, "mid": v(23.73, 5.73) * mm, "end": v(25.5, 5) * mm});
            skPoint(sketch, "E183.visualSharp", {"position": v(17, 5) * mm});
            skArc(sketch, "E183.filletArc", {"start": v(14.5, 5) * mm, "mid": v(16.27, 5.73) * mm, "end": v(17, 7.5) * mm});
            skPoint(sketch, "E184.visualSharp", {"position": v(11.5, 5) * mm});
            skArc(sketch, "E184.filletArc", {"start": v(11.5, 7.5) * mm, "mid": v(12.23, 5.73) * mm, "end": v(14, 5) * mm});
            skSolve(sketch);
        }
        {
            var Q0;
            Q0 = qSketchRegion(id + "F6", true);
            extrude(context, id + "F7", {"entities" : qUnion([Q0]), "operationType" : NewBodyOperationType.REMOVE, "oppositeDirection" : true, "depth" : 2.5 * mm});
        }
        {
            var Q0;
            Q0=makeQuery(id+"F7.boolean.opBoolean","COPY",FACE,{"derivedFrom":makeQuery(id+"F7.opExtrude","CAP_FACE",FACE,{"disambiguationData":[OSD([sQuery(id+"F6.wireOp",EDGE,"E75.0"),sQuery(id+"F6.wireOp",EDGE,"E75.1"),sQuery(id+"F6.wireOp",EDGE,"E75.2"),sQuery(id+"F6.wireOp",EDGE,"E75.3"),sQuery(id+"F6.wireOp",EDGE,"E75.4"),sQuery(id+"F6.wireOp",EDGE,"E75.5"),sQuery(id+"F6.wireOp",EDGE,"E75.6"),sQuery(id+"F6.wireOp",EDGE,"E75.7"),sQuery(id+"F6.wireOp",EDGE,"E76.0"),sQuery(id+"F6.wireOp",EDGE,"E77"),sQuery(id+"F6.wireOp",EDGE,"E78"),sQuery(id+"F6.wireOp",EDGE,"E79.0"),sQuery(id+"F6.wireOp",EDGE,"E79.1"),sQuery(id+"F6.wireOp",EDGE,"E79.2"),sQuery(id+"F6.wireOp",EDGE,"E79.3"),sQuery(id+"F6.wireOp",EDGE,"E79.4"),sQuery(id+"F6.wireOp",EDGE,"E80.0"),sQuery(id+"F6.wireOp",EDGE,"E80.1"),sQuery(id+"F6.wireOp",EDGE,"E80.2"),sQuery(id+"F6.wireOp",EDGE,"E80.3"),sQuery(id+"F6.wireOp",EDGE,"E80.4"),sQuery(id+"F6.wireOp",EDGE,"E81.0"),sQuery(id+"F6.wireOp",EDGE,"E81.1"),sQuery(id+"F6.wireOp",EDGE,"E81.2"),sQuery(id+"F6.wireOp",EDGE,"E81.3"),sQuery(id+"F6.wireOp",EDGE,"E81.4"),sQuery(id+"F6.wireOp",EDGE,"E82.0"),sQuery(id+"F6.wireOp",EDGE,"E82.1"),sQuery(id+"F6.wireOp",EDGE,"E82.2"),sQuery(id+"F6.wireOp",EDGE,"E82.3"),sQuery(id+"F6.wireOp",EDGE,"E82.4"),sQuery(id+"F6.wireOp",EDGE,"E83.0"),sQuery(id+"F6.wireOp",EDGE,"E83.1"),sQuery(id+"F6.wireOp",EDGE,"E83.2"),sQuery(id+"F6.wireOp",EDGE,"E84.0"),sQuery(id+"F6.wireOp",EDGE,"E84.1"),sQuery(id+"F6.wireOp",EDGE,"E84.2"),sQuery(id+"F6.wireOp",EDGE,"E85.0"),sQuery(id+"F6.wireOp",EDGE,"E85.1"),sQuery(id+"F6.wireOp",EDGE,"E85.2"),sQuery(id+"F6.wireOp",EDGE,"E86.0"),sQuery(id+"F6.wireOp",EDGE,"E86.1"),sQuery(id+"F6.wireOp",EDGE,"E86.2"),sQuery(id+"F6.wireOp",EDGE,"E87.0"),sQuery(id+"F6.wireOp",EDGE,"E87.1"),sQuery(id+"F6.wireOp",EDGE,"E87.2"),sQuery(id+"F6.wireOp",EDGE,"E88.0"),sQuery(id+"F6.wireOp",EDGE,"E88.1"),sQuery(id+"F6.wireOp",EDGE,"E88.2"),sQuery(id+"F6.wireOp",EDGE,"E89.0"),sQuery(id+"F6.wireOp",EDGE,"E89.1"),sQuery(id+"F6.wireOp",EDGE,"E89.2"),sQuery(id+"F6.wireOp",EDGE,"E90.0"),sQuery(id+"F6.wireOp",EDGE,"E90.1"),sQuery(id+"F6.wireOp",EDGE,"E90.2"),sQuery(id+"F6.wireOp",EDGE,"E91.0"),sQuery(id+"F6.wireOp",EDGE,"E91.1"),sQuery(id+"F6.wireOp",EDGE,"E91.2"),sQuery(id+"F6.wireOp",EDGE,"E92.0"),sQuery(id+"F6.wireOp",EDGE,"E92.1"),sQuery(id+"F6.wireOp",EDGE,"E92.2"),sQuery(id+"F6.wireOp",EDGE,"E93.0"),sQuery(id+"F6.wireOp",EDGE,"E93.1"),sQuery(id+"F6.wireOp",EDGE,"E93.2"),sQuery(id+"F6.wireOp",EDGE,"E94.0"),sQuery(id+"F6.wireOp",EDGE,"E94.1"),sQuery(id+"F6.wireOp",EDGE,"E94.2"),sQuery(id+"F6.wireOp",EDGE,"E95.0"),sQuery(id+"F6.wireOp",EDGE,"E95.1"),sQuery(id+"F6.wireOp",EDGE,"E95.2"),sQuery(id+"F6.wireOp",EDGE,"E96.0"),sQuery(id+"F6.wireOp",EDGE,"E96.1"),sQuery(id+"F6.wireOp",EDGE,"E96.2"),sQuery(id+"F6.wireOp",EDGE,"E98.trimOffspring"),sQuery(id+"F6.wireOp",EDGE,"E99.trimOffspring"),sQuery(id+"F6.wireOp",EDGE,"E100.trimOffspring"),sQuery(id+"F6.wireOp",EDGE,"E101.trimOffspring"),sQuery(id+"F6.wireOp",EDGE,"E102.trimOffspring"),sQuery(id+"F6.wireOp",EDGE,"E103.trimOffspring"),sQuery(id+"F6.wireOp",EDGE,"E104.trimOffspring"),sQuery(id+"F6.wireOp",EDGE,"E105.trimOffspring"),sQuery(id+"F6.wireOp",EDGE,"E106.trimOffspring"),sQuery(id+"F6.wireOp",EDGE,"E107.trimOffspring"),sQuery(id+"F6.wireOp",EDGE,"E108.trimOffspring"),sQuery(id+"F6.wireOp",EDGE,"E109.trimOffspring"),sQuery(id+"F6.wireOp",EDGE,"E110.trimOffspring"),sQuery(id+"F6.wireOp",EDGE,"E111.trimOffspring"),sQuery(id+"F6.wireOp",EDGE,"E112.trimOffspring"),sQuery(id+"F6.wireOp",EDGE,"E113.trimOffspring"),sQuery(id+"F6.wireOp",EDGE,"E114.0"),sQuery(id+"F6.wireOp",EDGE,"E114.1"),sQuery(id+"F6.wireOp",EDGE,"E114.2"),sQuery(id+"F6.wireOp",EDGE,"E115.trimOffspring"),sQuery(id+"F6.wireOp",EDGE,"E116.trimOffspring"),sQuery(id+"F6.wireOp",EDGE,"E117.filletArc"),sQuery(id+"F6.wireOp",EDGE,"E118.filletArc"),sQuery(id+"F6.wireOp",EDGE,"E119.filletArc"),sQuery(id+"F6.wireOp",EDGE,"E120.filletArc"),sQuery(id+"F6.wireOp",EDGE,"E121.filletArc"),sQuery(id+"F6.wireOp",EDGE,"E122.filletArc"),sQuery(id+"F6.wireOp",EDGE,"E123.filletArc"),sQuery(id+"F6.wireOp",EDGE,"E124.filletArc"),sQuery(id+"F6.wireOp",EDGE,"E125.filletArc"),sQuery(id+"F6.wireOp",EDGE,"E126.filletArc"),sQuery(id+"F6.wireOp",EDGE,"E127.filletArc"),sQuery(id+"F6.wireOp",EDGE,"E128.filletArc"),sQuery(id+"F6.wireOp",EDGE,"E129.filletArc"),sQuery(id+"F6.wireOp",EDGE,"E130.filletArc"),sQuery(id+"F6.wireOp",EDGE,"E131.filletArc"),sQuery(id+"F6.wireOp",EDGE,"E132.filletArc"),sQuery(id+"F6.wireOp",EDGE,"E133.filletArc"),sQuery(id+"F6.wireOp",EDGE,"E134.filletArc"),sQuery(id+"F6.wireOp",EDGE,"E135.filletArc"),sQuery(id+"F6.wireOp",EDGE,"E136.filletArc"),sQuery(id+"F6.wireOp",EDGE,"E137.filletArc"),sQuery(id+"F6.wireOp",EDGE,"E138.filletArc"),sQuery(id+"F6.wireOp",EDGE,"E139.filletArc"),sQuery(id+"F6.wireOp",EDGE,"E140.filletArc"),sQuery(id+"F6.wireOp",EDGE,"E141.filletArc"),sQuery(id+"F6.wireOp",EDGE,"E142.filletArc"),sQuery(id+"F6.wireOp",EDGE,"E143.filletArc"),sQuery(id+"F6.wireOp",EDGE,"E144.filletArc"),sQuery(id+"F6.wireOp",EDGE,"E145.filletArc"),sQuery(id+"F6.wireOp",EDGE,"E146.filletArc"),sQuery(id+"F6.wireOp",EDGE,"E147.filletArc"),sQuery(id+"F6.wireOp",EDGE,"E148.filletArc"),sQuery(id+"F6.wireOp",EDGE,"E149.filletArc"),sQuery(id+"F6.wireOp",EDGE,"E150.filletArc"),sQuery(id+"F6.wireOp",EDGE,"E151.filletArc"),sQuery(id+"F6.wireOp",EDGE,"E152.filletArc"),sQuery(id+"F6.wireOp",EDGE,"E153.filletArc"),sQuery(id+"F6.wireOp",EDGE,"E154.filletArc"),sQuery(id+"F6.wireOp",EDGE,"E155.filletArc"),sQuery(id+"F6.wireOp",EDGE,"E156.filletArc"),sQuery(id+"F6.wireOp",EDGE,"E157.filletArc"),sQuery(id+"F6.wireOp",EDGE,"E158.filletArc"),sQuery(id+"F6.wireOp",EDGE,"E159.filletArc"),sQuery(id+"F6.wireOp",EDGE,"E160.filletArc"),sQuery(id+"F6.wireOp",EDGE,"E161.filletArc"),sQuery(id+"F6.wireOp",EDGE,"E162.filletArc"),sQuery(id+"F6.wireOp",EDGE,"E163.filletArc"),sQuery(id+"F6.wireOp",EDGE,"E164.filletArc"),sQuery(id+"F6.wireOp",EDGE,"E165.filletArc"),sQuery(id+"F6.wireOp",EDGE,"E166.filletArc"),sQuery(id+"F6.wireOp",EDGE,"E167.filletArc"),sQuery(id+"F6.wireOp",EDGE,"E168.filletArc"),sQuery(id+"F6.wireOp",EDGE,"E169.filletArc"),sQuery(id+"F6.wireOp",EDGE,"E170.filletArc"),sQuery(id+"F6.wireOp",EDGE,"E171.filletArc"),sQuery(id+"F6.wireOp",EDGE,"E172.filletArc"),sQuery(id+"F6.wireOp",EDGE,"E173.filletArc"),sQuery(id+"F6.wireOp",EDGE,"E174.filletArc"),sQuery(id+"F6.wireOp",EDGE,"E175.filletArc"),sQuery(id+"F6.wireOp",EDGE,"E176.filletArc"),sQuery(id+"F6.wireOp",EDGE,"E177.filletArc"),sQuery(id+"F6.wireOp",EDGE,"E178.filletArc"),sQuery(id+"F6.wireOp",EDGE,"E179.filletArc"),sQuery(id+"F6.wireOp",EDGE,"E180.filletArc"),sQuery(id+"F6.wireOp",EDGE,"E181.filletArc"),sQuery(id+"F6.wireOp",EDGE,"E182.filletArc"),sQuery(id+"F6.wireOp",EDGE,"E183.filletArc"),sQuery(id+"F6.wireOp",EDGE,"E184.filletArc")])],"isStart":false})});
            fillet(context, id + "F8", {"entities" : qUnion([Q0]), "radius" : 2.5 * mm, "tangentPropagation" : true, "allowEdgeOverflow" : false});
        }
        {
            var Q0;
            Q0=makeQuery(id+"F3.boolean.opBoolean","COPY",FACE,{"derivedFrom":makeQuery(id+"F3.opExtrude","CAP_FACE",FACE,{"disambiguationData":[OSD([sQuery(id+"F2.wireOp",EDGE,"E5.0"),sQuery(id+"F2.wireOp",EDGE,"E5.1"),sQuery(id+"F2.wireOp",EDGE,"E5.2"),sQuery(id+"F2.wireOp",EDGE,"E5.3"),sQuery(id+"F2.wireOp",EDGE,"E5.4"),sQuery(id+"F2.wireOp",EDGE,"E5.5"),sQuery(id+"F2.wireOp",EDGE,"E5.6"),sQuery(id+"F2.wireOp",EDGE,"E5.7"),sQuery(id+"F2.wireOp",EDGE,"E6"),sQuery(id+"F2.wireOp",EDGE,"E7.0"),sQuery(id+"F2.wireOp",EDGE,"E8.0"),sQuery(id+"F2.wireOp",EDGE,"E9.0"),sQuery(id+"F2.wireOp",EDGE,"E10.0"),sQuery(id+"F2.wireOp",EDGE,"E11.0"),sQuery(id+"F2.wireOp",EDGE,"E12.trimOffspring"),sQuery(id+"F2.wireOp",EDGE,"E13.trimOffspring"),sQuery(id+"F2.wireOp",EDGE,"E14.trimOffspring"),sQuery(id+"F2.wireOp",EDGE,"E15.trimOffspring"),sQuery(id+"F2.wireOp",EDGE,"E16.trimOffspring"),sQuery(id+"F2.wireOp",EDGE,"E17.trimOffspring"),sQuery(id+"F2.wireOp",EDGE,"E18.trimOffspring"),sQuery(id+"F2.wireOp",EDGE,"E19.trimOffspring"),sQuery(id+"F2.wireOp",EDGE,"E20.trimOffspring"),sQuery(id+"F2.wireOp",EDGE,"E21.trimOffspring"),sQuery(id+"F2.wireOp",EDGE,"E22"),sQuery(id+"F2.wireOp",EDGE,"E23.0"),sQuery(id+"F2.wireOp",EDGE,"E24.0"),sQuery(id+"F2.wireOp",EDGE,"E25.0"),sQuery(id+"F2.wireOp",EDGE,"E26.0"),sQuery(id+"F2.wireOp",EDGE,"E27.0"),sQuery(id+"F2.wireOp",EDGE,"E28.trimOffspring"),sQuery(id+"F2.wireOp",EDGE,"E29.trimOffspring"),sQuery(id+"F2.wireOp",EDGE,"E30.trimOffspring"),sQuery(id+"F2.wireOp",EDGE,"E31.trimOffspring"),sQuery(id+"F2.wireOp",EDGE,"E32.trimOffspring"),sQuery(id+"F2.wireOp",EDGE,"E33.trimOffspring"),sQuery(id+"F2.wireOp",EDGE,"E34.trimOffspring"),sQuery(id+"F2.wireOp",EDGE,"E35.trimOffspring"),sQuery(id+"F2.wireOp",EDGE,"E36.trimOffspring"),sQuery(id+"F2.wireOp",EDGE,"E37.trimOffspring"),sQuery(id+"F2.wireOp",EDGE,"E38.filletArc"),sQuery(id+"F2.wireOp",EDGE,"E39.filletArc"),sQuery(id+"F2.wireOp",EDGE,"E40.filletArc"),sQuery(id+"F2.wireOp",EDGE,"E41.filletArc"),sQuery(id+"F2.wireOp",EDGE,"E42.filletArc"),sQuery(id+"F2.wireOp",EDGE,"E43.filletArc"),sQuery(id+"F2.wireOp",EDGE,"E44.filletArc"),sQuery(id+"F2.wireOp",EDGE,"E45.filletArc"),sQuery(id+"F2.wireOp",EDGE,"E46.filletArc"),sQuery(id+"F2.wireOp",EDGE,"E47.filletArc"),sQuery(id+"F2.wireOp",EDGE,"E48.filletArc"),sQuery(id+"F2.wireOp",EDGE,"E49.filletArc"),sQuery(id+"F2.wireOp",EDGE,"E50.filletArc"),sQuery(id+"F2.wireOp",EDGE,"E51.filletArc"),sQuery(id+"F2.wireOp",EDGE,"E52.filletArc"),sQuery(id+"F2.wireOp",EDGE,"E53.filletArc"),sQuery(id+"F2.wireOp",EDGE,"E54.filletArc"),sQuery(id+"F2.wireOp",EDGE,"E55.filletArc"),sQuery(id+"F2.wireOp",EDGE,"E56.filletArc"),sQuery(id+"F2.wireOp",EDGE,"E57.filletArc"),sQuery(id+"F2.wireOp",EDGE,"E58.filletArc"),sQuery(id+"F2.wireOp",EDGE,"E59.filletArc"),sQuery(id+"F2.wireOp",EDGE,"E60.filletArc"),sQuery(id+"F2.wireOp",EDGE,"E61.filletArc"),sQuery(id+"F2.wireOp",EDGE,"E62.filletArc"),sQuery(id+"F2.wireOp",EDGE,"E63.filletArc"),sQuery(id+"F2.wireOp",EDGE,"E64.filletArc"),sQuery(id+"F2.wireOp",EDGE,"E65.filletArc"),sQuery(id+"F2.wireOp",EDGE,"E66.filletArc"),sQuery(id+"F2.wireOp",EDGE,"E67.filletArc"),sQuery(id+"F2.wireOp",EDGE,"E68.filletArc"),sQuery(id+"F2.wireOp",EDGE,"E69.filletArc")])],"isStart":false})});
            fillet(context, id + "F9", {"entities" : qUnion([Q0]), "radius" : 2.5 * mm, "tangentPropagation" : true, "allowEdgeOverflow" : false});
        }
    });
